# Revit family: Sink-Bradley_Corp-Omnideck_LD-5010_WashBar_1Bowl
name_source: partatom
category: Plumbing Fixtures
revit_build: Autodesk Revit 2017 (Build: 20160225_1515(x64)
units: mm (PartAtom-declared; Revit-internal decimal feet)

## family parameters
Always vertical = Yes
Cut with Voids When Loaded = No
OmniClass Number = 23.45.00.00
OmniClass Title = Sanitary, Laundry, and Cleaning Equipment
Part Type = Normal
Room Calculation Point = No
Round Connector Dimension = Use Diameter
Shared = No
Work Plane-Based = No

## types (1)
- Omnideck LD-5010 WashBar 1-Bowl
    Assembly Code = D2010400
    Description = Bradley Omnideck Lavatory LD 3010  - HS TS1 Two  Bowl
    Manufacturer = Bradley Corporation
    Manufacturer Installation URL - English = https://www.bradleycorp.com
    MasterFormat Number = 22 42 16
    MasterFormat Title = Commercial Lavatories and Sinks
    Model = LD 3010 HS TS1 2-Bowl
    OmniClass Table 23 Number = 23.45 05 14 14
    OmniClass Table 23 Title = Sinks/Lavatories
    Product Page URL = https://www.bradleycorp.com
    Product Tech Data URL - English = https://www.bradleycorp.com
    Specifications URL = https://www.bradleycorp.com
    URL = http://bradleycorp.com

## geometry (parser evidence)
native form markers: Blend x12, Sweep x18
no freeform markers — native parametric forms only
